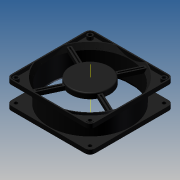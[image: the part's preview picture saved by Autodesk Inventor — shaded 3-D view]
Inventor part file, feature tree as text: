
AUTODESK INVENTOR PART (.ipt)
format: ipt  version: 2013 (Build 170138000, 138)  size: 356,864 bytes
history: native  units: mm (DEFAULTED — no unit token found)
features: sketch x11, extrude x7, fillet x3, plane x2, pattern_circular x2, revolve x1, hole x1, other x1, mirror x1
ambient origin geometry x8: Origin, YZ Plane, XZ Plane, XY Plane, X Axis, Y Axis, Z Axis, Center Point
bodies: Solid1 (feature_tree)
feature tree (29):
  revolve  "Revolution1"  [1 undecoded]
  plane  "Work Plane1"
  sketch  "Sketch2"  dims[d2=150.0deg d3=7.112mm]
  extrude  "Extrusion1"  Depth=7.112mm
  sketch  "Sketch3"  dims[d4=38.1mm d5=4.572mm d6=114.3mm d7=90.0deg]
  extrude  "Extrusion4"  Depth=4.572mm
  fillet  "Fillet2"  Radius=114.3mm
  fillet  "Fillet3"  [1 undecoded]
  extrude  "Extrusion5"  Depth=118.872mm
  extrude  "Extrusion6"  Depth=59.436mm
  hole  "Hole1"  [1 undecoded]
  other  "Work Axis1"
  pattern_circular  "Circular Pattern1"  [2 undecoded]
  mirror  "Mirror1"
  extrude  "Extrusion7"  Depth=5.08mm
  fillet  "Fillet4"  Radius=7.112mm
  sketch  "Sketch13"  dims[d17=1.016mm]
  plane  "Work Plane4"
  extrude  "Extrusion8"  Depth=0.762mm TaperAngle=0.0deg
  extrude  "Extrusion9"  Depth=7.62mm
  pattern_circular  "Circular Pattern2"  [2 undecoded]
  sketch  "Sketch1"  dims[d0=1.016mm d1=1.016mm]
  sketch  "Sketch6"  dims[d8=-19.05mm d9=118.872mm]
  sketch  "Sketch7"  dims[d10=118.872mm d11=59.436mm]
  sketch  "Sketch8"  dims[d12=59.436mm d13=25.4mm d14=0.0mm]
  sketch  "Sketch9"  dims[d15=1.016mm]
  sketch  "Sketch10"  dims[d16=1.016mm]
  sketch  "Sketch14"  dims[d18=1.016mm]
  sketch  "Sketch15"  dims[d27=1.778mm d28=6.096mm d29=0.0mm d30=5.08mm d31=7.112mm d32=0.762mm d33=0.0mm d34=7.62mm d35=4.7498mm d36=0.0mm d37=4.7498mm d38=12.7mm d39=9.525mm d40=6.35mm d41=14.3117mm d42=19.05mm d43=20.594885mm d44=40.0mm d46=360.0deg d47=55.88mm d48=7.62mm d49=0.0mm d50=1.524mm d51=5.588mm d52=3.048mm d53=5.588mm d54=3.048mm d55=0.0mm d56=3.048mm d57=0.0mm d58=40.0mm d60=360.0deg]
note: 7 required parameter values undecoded (feature->parameter linkage not recoverable at this tier; creation-order binding heuristic only, values carry confidence <= 0.55)